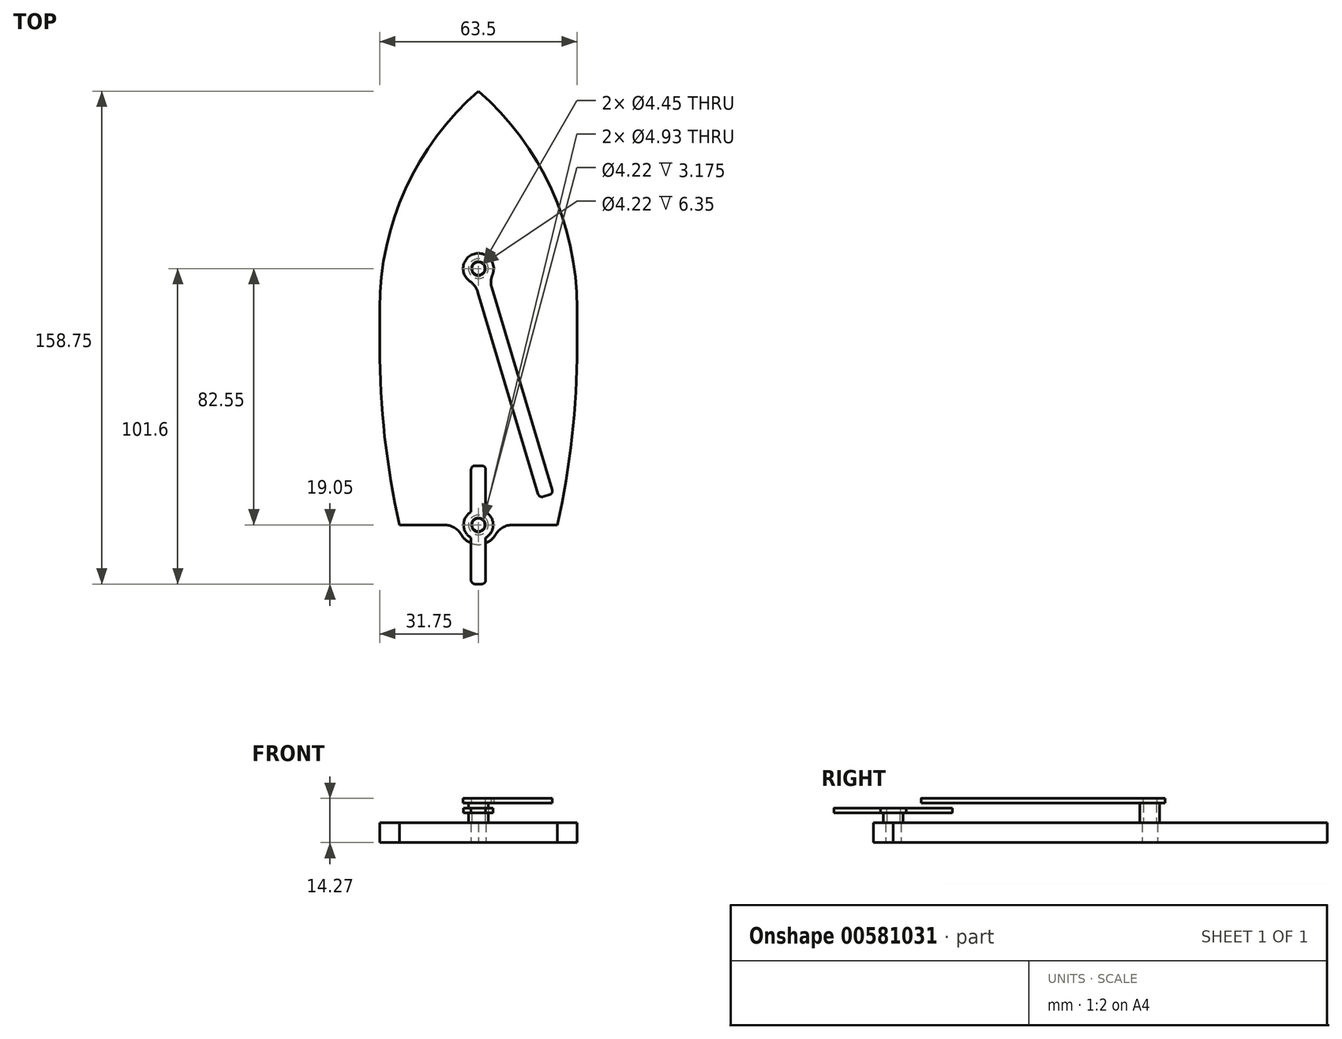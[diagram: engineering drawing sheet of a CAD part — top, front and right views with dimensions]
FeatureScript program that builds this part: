
annotation { "Feature Type Name" : "Feature", "Feature Type Description" : "" }
export const myFeature = defineFeature(function(context is Context, id is Id, definition is map)
    precondition{}
    {
        {
            var Q0;
            Q0=qCreatedBy(makeId("Top.planeOp"),FACE);
            var sketch = newSketch(context, id + "F0", { "sketchPlane" : qUnion([Q0])});
            skPoint(sketch, "E0.rect.middle", {"position": v(0, 0) * mm});
            skCircle(sketch, "E1", {"center": v(0, 12.7) * mm, "radius": 2.46 * mm});
            skPoint(sketch, "E2.endSnap0", {"position": v(-31.75, 0) * mm});
            skArc(sketch, "E3", {"start": v(-31.75, 0) * mm, "mid": v(-23.44, 38.36) * mm, "end": v(0, 69.85) * mm});
            skLineSegment(sketch, "E4", {"start": v(-31.75, 0) * mm, "end": v(-31.75, -12.7) * mm});
            skArc(sketch, "E5", {"start": v(-31.75, -12.7) * mm, "mid": v(-30.16, -41.45) * mm, "end": v(-25.4, -69.85) * mm});
            skLineSegment(sketch, "E6", {"start": v(-25.4, -69.85) * mm, "end": v(-11, -69.85) * mm});
            skArc(sketch, "E7.MirrorCS", {"start": v(31.75, 0) * mm, "mid": v(23.44, 38.36) * mm, "end": v(0, 69.85) * mm});
            skArc(sketch, "E8.MirrorCS", {"start": v(31.75, -12.7) * mm, "mid": v(30.16, -41.45) * mm, "end": v(25.4, -69.85) * mm});
            skLineSegment(sketch, "E9.MirrorCS", {"start": v(31.75, 0) * mm, "end": v(31.75, -12.7) * mm});
            skArc(sketch, "E10", {"start": v(-5.5, -73.03) * mm, "mid": v(0, -76.2) * mm, "end": v(5.5, -73.03) * mm});
            skCircle(sketch, "E11", {"center": v(0, -69.85) * mm, "radius": 2.46 * mm});
            skLineSegment(sketch, "E12.trimOffspring", {"start": v(11, -69.85) * mm, "end": v(25.4, -69.85) * mm});
            skLineSegment(sketch, "E13", {"start": v(-6.35, -69.85) * mm, "end": v(6.35, -69.85) * mm, "construction": true});
            skLineSegment(sketch, "E14", {"start": v(0, 0) * mm, "end": v(0, -85.3) * mm, "construction": true});
            skPoint(sketch, "E14.endSnap0", {"position": v(0, -76.2) * mm});
            skPoint(sketch, "E15.visualSharp", {"position": v(-6.35, -69.85) * mm});
            skArc(sketch, "E15.filletArc", {"start": v(-5.5, -73.03) * mm, "mid": v(-7.82, -70.7) * mm, "end": v(-11, -69.85) * mm});
            skPoint(sketch, "E16.visualSharp", {"position": v(6.35, -69.85) * mm});
            skArc(sketch, "E16.filletArc", {"start": v(11, -69.85) * mm, "mid": v(7.82, -70.7) * mm, "end": v(5.5, -73.03) * mm});
            skSolve(sketch);
        }
        {
            var Q0;
            Q0=makeQuery(id+"F0.imprint","IMPRINT",FACE,{"disambiguationData":[TD([[makeQuery(id+"F0.imprint","IMPRINT",EDGE,{"derivedFrom":sQuery(id+"F0.wireOp",EDGE,"E1")}),-1.0]])]});
            extrude(context, id + "F1", {"entities" : qUnion([Q0]), "depth" : 6.35 * mm});
        }
        {
            var Q0;
            Q0=makeQuery(id+"F1.opExtrude","CAP_FACE",FACE,{"disambiguationData":[OSD([sQuery(id+"F0.wireOp",EDGE,"E1"),sQuery(id+"F0.wireOp",EDGE,"E3"),sQuery(id+"F0.wireOp",EDGE,"E4"),sQuery(id+"F0.wireOp",EDGE,"E5"),sQuery(id+"F0.wireOp",EDGE,"E6"),sQuery(id+"F0.wireOp",EDGE,"E7.MirrorCS"),sQuery(id+"F0.wireOp",EDGE,"E8.MirrorCS"),sQuery(id+"F0.wireOp",EDGE,"E9.MirrorCS"),sQuery(id+"F0.wireOp",EDGE,"E10"),sQuery(id+"F0.wireOp",EDGE,"E11"),sQuery(id+"F0.wireOp",EDGE,"E12.trimOffspring"),sQuery(id+"F0.wireOp",EDGE,"E15.filletArc"),sQuery(id+"F0.wireOp",EDGE,"E16.filletArc")])],"isStart":false});
            var sketch = newSketch(context, id + "F2", { "sketchPlane" : qUnion([Q0])});
            skCircle(sketch, "E17", {"center": v(0, 12.7) * mm, "radius": 2.1 * mm});
            skCircle(sketch, "E18", {"center": v(0, 12.7) * mm, "radius": 3.18 * mm});
            skSolve(sketch);
        }
        {
            var Q0;
            Q0=qSketchRegion(id+"F2",true);
            extrude(context, id + "F3", {"entities" : qUnion([Q0]), "depth" : 6.35 * mm});
        }
        {
            var Q0;
            Q0=makeQuery(id+"F1.opExtrude","CAP_FACE",FACE,{"disambiguationData":[OSD([sQuery(id+"F0.wireOp",EDGE,"E1"),sQuery(id+"F0.wireOp",EDGE,"E3"),sQuery(id+"F0.wireOp",EDGE,"E4"),sQuery(id+"F0.wireOp",EDGE,"E5"),sQuery(id+"F0.wireOp",EDGE,"E6"),sQuery(id+"F0.wireOp",EDGE,"E7.MirrorCS"),sQuery(id+"F0.wireOp",EDGE,"E8.MirrorCS"),sQuery(id+"F0.wireOp",EDGE,"E9.MirrorCS"),sQuery(id+"F0.wireOp",EDGE,"E10"),sQuery(id+"F0.wireOp",EDGE,"E11"),sQuery(id+"F0.wireOp",EDGE,"E12.trimOffspring"),sQuery(id+"F0.wireOp",EDGE,"E15.filletArc"),sQuery(id+"F0.wireOp",EDGE,"E16.filletArc")])],"isStart":false});
            var sketch = newSketch(context, id + "F4", { "sketchPlane" : qUnion([Q0])});
            skCircle(sketch, "E19", {"center": v(0, -69.85) * mm, "radius": 3.17 * mm});
            skCircle(sketch, "E20", {"center": v(0, -69.85) * mm, "radius": 2.1 * mm});
            skSolve(sketch);
        }
        {
            var Q0;
            Q0=qSketchRegion(id+"F4",true);
            extrude(context, id + "F5", {"entities" : qUnion([Q0]), "depth" : 3.17 * mm});
        }
        {
            var Q0;
            Q0=makeQuery(id+"F3.opExtrude","CAP_FACE",FACE,{"disambiguationData":[OSD([sQuery(id+"F2.wireOp",EDGE,"E17"),sQuery(id+"F2.wireOp",EDGE,"E18")])],"isStart":false});
            var sketch = newSketch(context, id + "F6", { "sketchPlane" : qUnion([Q0])});
            skArc(sketch, "E21", {"start": v(4.53, 10.8) * mm, "mid": v(-1.4, 17.4) * mm, "end": v(-2.75, 8.63) * mm});
            skLineSegment(sketch, "E22", {"start": v(0, 12.7) * mm, "end": v(23.42, -65.72) * mm, "construction": true});
            skLineSegment(sketch, "E23.0", {"start": v(-0.22, 5.18) * mm, "end": v(19.23, -59.93) * mm});
            skLineSegment(sketch, "E24.0", {"start": v(4.3, 6.53) * mm, "end": v(23.75, -58.58) * mm});
            skCircle(sketch, "E25", {"center": v(0, 12.7) * mm, "radius": 2.22 * mm});
            skLineSegment(sketch, "E26", {"start": v(20.8, -60.78) * mm, "end": v(22.9, -60.16) * mm});
            skPoint(sketch, "E27.visualSharp", {"position": v(-1.03, 7.9) * mm});
            skArc(sketch, "E27.filletArc", {"start": v(-0.22, 5.18) * mm, "mid": v(-1.19, 7.12) * mm, "end": v(-2.75, 8.63) * mm});
            skPoint(sketch, "E28.visualSharp", {"position": v(3.5, 9.25) * mm});
            skArc(sketch, "E28.filletArc", {"start": v(4.53, 10.8) * mm, "mid": v(4.05, 8.69) * mm, "end": v(4.3, 6.53) * mm});
            skPoint(sketch, "E29.visualSharp", {"position": v(24.12, -59.8) * mm});
            skArc(sketch, "E29.filletArc", {"start": v(22.9, -60.16) * mm, "mid": v(23.65, -59.55) * mm, "end": v(23.75, -58.58) * mm});
            skPoint(sketch, "E30.visualSharp", {"position": v(19.59, -61.15) * mm});
            skArc(sketch, "E30.filletArc", {"start": v(19.23, -59.93) * mm, "mid": v(19.84, -60.68) * mm, "end": v(20.8, -60.78) * mm});
            skSolve(sketch);
        }
        {
            var Q0;
            Q0=makeQuery(id+"F6.imprint","IMPRINT",FACE,{"disambiguationData":[TD([[makeQuery(id+"F6.imprint","IMPRINT",EDGE,{"derivedFrom":sQuery(id+"F6.wireOp",EDGE,"E25")}),-1.0]])]});
            var Q1;
            Q1=makeQuery(id+"F6.imprint","IMPRINT",FACE,{"disambiguationData":[TD([[makeQuery(id+"F6.imprint","IMPRINT",EDGE,{"derivedFrom":sQuery(id+"F6.wireOp",EDGE,"E21")}),1.0]])]});
            extrude(context, id + "F7", {"entities" : qUnion([Q0, Q1]), "depth" : 1.57 * mm});
        }
        {
            var Q0;
            Q0=makeQuery(id+"F5.opExtrude","CAP_FACE",FACE,{"disambiguationData":[OSD([sQuery(id+"F4.wireOp",EDGE,"E19"),sQuery(id+"F4.wireOp",EDGE,"E20")])],"isStart":false});
            var sketch = newSketch(context, id + "F8", { "sketchPlane" : qUnion([Q0])});
            skCircle(sketch, "E31", {"center": v(0, -69.85) * mm, "radius": 2.22 * mm});
            skArc(sketch, "E32", {"start": v(-2.36, -65.71) * mm, "mid": v(-4.76, -69.85) * mm, "end": v(-2.36, -73.99) * mm});
            skLineSegment(sketch, "E33", {"start": v(0, -69.85) * mm, "end": v(0, -87.87) * mm, "construction": true});
            skLineSegment(sketch, "E34.0", {"start": v(-2.36, -52.07) * mm, "end": v(-2.36, -65.71) * mm});
            skLineSegment(sketch, "E35.0", {"start": v(2.36, -52.07) * mm, "end": v(2.36, -65.71) * mm});
            skLineSegment(sketch, "E36", {"start": v(-1.1, -88.9) * mm, "end": v(1.1, -88.9) * mm});
            skLineSegment(sketch, "E37.0", {"start": v(-1.1, -50.8) * mm, "end": v(1.1, -50.8) * mm});
            skLineSegment(sketch, "E38.trimOffspring", {"start": v(2.36, -73.99) * mm, "end": v(2.36, -87.63) * mm});
            skLineSegment(sketch, "E39.trimOffspring", {"start": v(-2.36, -73.99) * mm, "end": v(-2.36, -87.63) * mm});
            skArc(sketch, "E40.trimOffspring", {"start": v(2.36, -73.99) * mm, "mid": v(4.76, -69.85) * mm, "end": v(2.36, -65.71) * mm});
            skPoint(sketch, "E41.visualSharp", {"position": v(-2.36, -50.8) * mm});
            skArc(sketch, "E41.filletArc", {"start": v(-1.1, -50.8) * mm, "mid": v(-2, -51.17) * mm, "end": v(-2.36, -52.07) * mm});
            skPoint(sketch, "E42.visualSharp", {"position": v(2.36, -50.8) * mm});
            skArc(sketch, "E42.filletArc", {"start": v(2.36, -52.07) * mm, "mid": v(2, -51.17) * mm, "end": v(1.1, -50.8) * mm});
            skPoint(sketch, "E43.visualSharp", {"position": v(2.36, -88.9) * mm});
            skArc(sketch, "E43.filletArc", {"start": v(1.1, -88.9) * mm, "mid": v(2, -88.53) * mm, "end": v(2.36, -87.63) * mm});
            skPoint(sketch, "E44.visualSharp", {"position": v(-2.36, -88.9) * mm});
            skArc(sketch, "E44.filletArc", {"start": v(-2.36, -87.63) * mm, "mid": v(-2, -88.53) * mm, "end": v(-1.1, -88.9) * mm});
            skSolve(sketch);
        }
        {
            var Q0;
            Q0=qSketchRegion(id+"F8",true);
            extrude(context, id + "F9", {"entities" : qUnion([Q0]), "depth" : 1.57 * mm});
        }
    });
